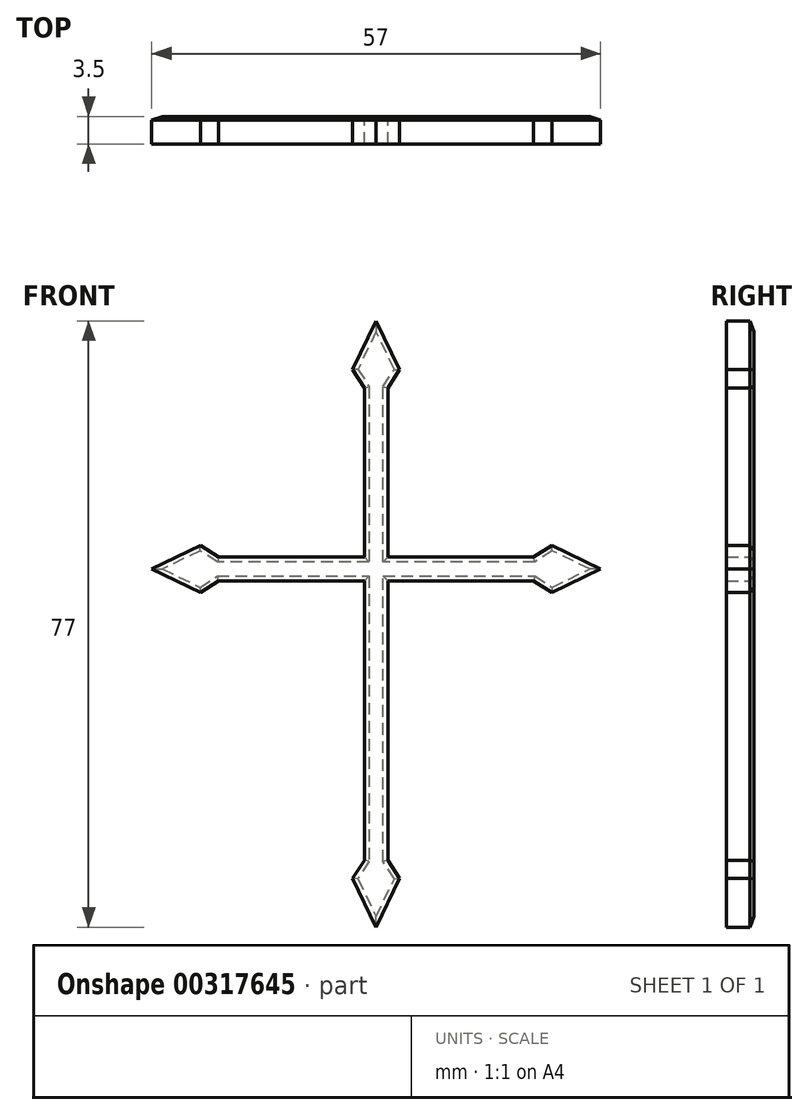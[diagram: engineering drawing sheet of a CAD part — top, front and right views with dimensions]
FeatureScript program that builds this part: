
annotation { "Feature Type Name" : "Feature", "Feature Type Description" : "" }
export const myFeature = defineFeature(function(context is Context, id is Id, definition is map)
    precondition{}
    {
        {
            var Q0;
            Q0=qCreatedBy(makeId("Front.planeOp"),FACE);
            var sketch = newSketch(context, id + "F0", { "sketchPlane" : qUnion([Q0])});
            skLineSegment(sketch, "E0", {"start": v(-20, 1.5) * mm, "end": v(-1.5, 1.5) * mm});
            skLineSegment(sketch, "E1.MirrorCS", {"start": v(-20, -1.5) * mm, "end": v(-1.5, -1.5) * mm});
            skLineSegment(sketch, "E2", {"start": v(-1.5, 23) * mm, "end": v(-1.5, 1.5) * mm});
            skLineSegment(sketch, "E3", {"start": v(1.5, -37) * mm, "end": v(1.5, -1.5) * mm});
            skLineSegment(sketch, "E4", {"start": v(20, -1.5) * mm, "end": v(22.33, -3) * mm});
            skLineSegment(sketch, "E5.MirrorCS", {"start": v(20, 1.5) * mm, "end": v(22.33, 3) * mm});
            skLineSegment(sketch, "E6", {"start": v(22.33, 3) * mm, "end": v(28.5, 0) * mm});
            skLineSegment(sketch, "E7.MirrorCS", {"start": v(22.33, -3) * mm, "end": v(28.5, 0) * mm});
            skLineSegment(sketch, "E8.MirrorCS", {"start": v(-20, 1.5) * mm, "end": v(-22.33, 3) * mm});
            skLineSegment(sketch, "E9.MirrorCS", {"start": v(-20, -1.5) * mm, "end": v(-22.33, -3) * mm});
            skLineSegment(sketch, "E10.MirrorCS", {"start": v(-22.33, -3) * mm, "end": v(-28.5, 0) * mm});
            skLineSegment(sketch, "E11.MirrorCS", {"start": v(-22.33, 3) * mm, "end": v(-28.5, 0) * mm});
            skLineSegment(sketch, "E12", {"start": v(-1.5, 23) * mm, "end": v(-3, 25.33) * mm});
            skLineSegment(sketch, "E13", {"start": v(-3, 25.33) * mm, "end": v(0, 31.5) * mm});
            skLineSegment(sketch, "E14.MirrorCS", {"start": v(1.5, 23) * mm, "end": v(3, 25.33) * mm});
            skLineSegment(sketch, "E15.MirrorCS", {"start": v(3, 25.33) * mm, "end": v(0, 31.5) * mm});
            skLineSegment(sketch, "E16", {"start": v(-20, -7) * mm, "end": v(19.26, -7) * mm, "construction": true});
            skLineSegment(sketch, "E17.MirrorCS", {"start": v(-1.5, -37) * mm, "end": v(-3, -39.33) * mm});
            skLineSegment(sketch, "E18.MirrorCS", {"start": v(-3, -39.33) * mm, "end": v(0, -45.5) * mm});
            skLineSegment(sketch, "E19.MirrorCS", {"start": v(3, -39.33) * mm, "end": v(0, -45.5) * mm});
            skLineSegment(sketch, "E20.MirrorCS", {"start": v(1.5, -37) * mm, "end": v(3, -39.33) * mm});
            skLineSegment(sketch, "E21.trimOffspring", {"start": v(-1.5, -1.5) * mm, "end": v(-1.5, -37) * mm});
            skLineSegment(sketch, "E22.trimOffspring", {"start": v(1.5, 1.5) * mm, "end": v(20, 1.5) * mm});
            skLineSegment(sketch, "E23.trimOffspring", {"start": v(1.5, 1.5) * mm, "end": v(1.5, 23) * mm});
            skLineSegment(sketch, "E24.trimOffspring", {"start": v(1.5, -1.5) * mm, "end": v(20, -1.5) * mm});
            skLineSegment(sketch, "E25", {"start": v(-1.5, -1) * mm, "end": v(-20, -1) * mm});
            skLineSegment(sketch, "E26.MirrorCS", {"start": v(-1.5, 1) * mm, "end": v(-20, 1) * mm});
            skLineSegment(sketch, "E27.MirrorCS", {"start": v(1.5, -1) * mm, "end": v(20, -1) * mm});
            skLineSegment(sketch, "E28.MirrorCS", {"start": v(1.5, 1) * mm, "end": v(20, 1) * mm});
            skLineSegment(sketch, "E29", {"start": v(-1, -1.5) * mm, "end": v(-1, -37) * mm});
            skLineSegment(sketch, "E30", {"start": v(-1, -37) * mm, "end": v(-2.5, -39.33) * mm});
            skLineSegment(sketch, "E31", {"start": v(-2.5, -39.33) * mm, "end": v(0, -44.47) * mm});
            skLineSegment(sketch, "E32", {"start": v(0, -44.47) * mm, "end": v(2.5, -39.33) * mm});
            skLineSegment(sketch, "E33", {"start": v(2.5, -39.33) * mm, "end": v(1, -37) * mm});
            skLineSegment(sketch, "E34", {"start": v(1, -37) * mm, "end": v(1, -1) * mm});
            skLineSegment(sketch, "E35", {"start": v(1, -1) * mm, "end": v(1.5, -1) * mm});
            skLineSegment(sketch, "E36", {"start": v(-1, -1.5) * mm, "end": v(-1, -1) * mm});
            skLineSegment(sketch, "E37", {"start": v(-1, -1) * mm, "end": v(-1.5, -1) * mm});
            skLineSegment(sketch, "E38", {"start": v(-20, -1) * mm, "end": v(-22.33, -2.5) * mm});
            skLineSegment(sketch, "E39", {"start": v(-22.33, -2.5) * mm, "end": v(-27.47, 0) * mm});
            skLineSegment(sketch, "E40", {"start": v(-27.47, 0) * mm, "end": v(-22.33, 2.5) * mm});
            skLineSegment(sketch, "E41", {"start": v(-22.33, 2.5) * mm, "end": v(-20, 1) * mm});
            skLineSegment(sketch, "E42", {"start": v(-1.5, 1) * mm, "end": v(-1, 1) * mm});
            skLineSegment(sketch, "E43", {"start": v(-1, 1) * mm, "end": v(-1, 23) * mm});
            skLineSegment(sketch, "E44", {"start": v(-1, 23) * mm, "end": v(-2.5, 25.33) * mm});
            skLineSegment(sketch, "E45", {"start": v(-2.5, 25.33) * mm, "end": v(0, 30.47) * mm});
            skLineSegment(sketch, "E46", {"start": v(0, 30.47) * mm, "end": v(2.5, 25.33) * mm});
            skLineSegment(sketch, "E47", {"start": v(2.5, 25.33) * mm, "end": v(1, 23) * mm});
            skLineSegment(sketch, "E48", {"start": v(1, 23) * mm, "end": v(1, 1) * mm});
            skLineSegment(sketch, "E49", {"start": v(1, 1) * mm, "end": v(1.5, 1) * mm});
            skLineSegment(sketch, "E50", {"start": v(20, 1) * mm, "end": v(22.33, 2.5) * mm});
            skLineSegment(sketch, "E51", {"start": v(22.33, 2.5) * mm, "end": v(27.47, 0) * mm});
            skLineSegment(sketch, "E52", {"start": v(27.47, 0) * mm, "end": v(22.33, -2.5) * mm});
            skLineSegment(sketch, "E53", {"start": v(22.33, -2.5) * mm, "end": v(20, -1) * mm});
            skSolve(sketch);
        }
        {
            var Q0;
            Q0=makeQuery(id+"F0.imprint","IMPRINT",FACE,{"disambiguationData":[TD([[makeQuery(id+"F0.imprint","IMPRINT",EDGE,{"derivedFrom":sQuery(id+"F0.wireOp",EDGE,"E25")}),-1.0]])]});
            var Q1;
            Q1=makeQuery(id+"F0.imprint","IMPRINT",FACE,{"disambiguationData":[TD([[makeQuery(id+"F0.imprint","IMPRINT",EDGE,{"derivedFrom":sQuery(id+"F0.wireOp",EDGE,"E0")}),-1.0]])]});
            extrude(context, id + "F1", {"entities" : qUnion([Q0, Q1]), "depth" : 1.5 * mm});
        }
        {
            var Q0;
            Q0=makeQuery(id+"F0.imprint","IMPRINT",FACE,{"disambiguationData":[TD([[makeQuery(id+"F0.imprint","IMPRINT",EDGE,{"derivedFrom":sQuery(id+"F0.wireOp",EDGE,"E0")}),-1.0]])]});
            var Q1;
            Q1=makeQuery(id+"F0.imprint","IMPRINT",FACE,{"disambiguationData":[TD([[makeQuery(id+"F0.imprint","IMPRINT",EDGE,{"derivedFrom":sQuery(id+"F0.wireOp",EDGE,"E25")}),-1.0]])]});
            extrude(context, id + "F2", {"entities" : qUnion([Q0, Q1]), "operationType" : NewBodyOperationType.ADD, "oppositeDirection" : true, "depth" : 0.5 * mm, "hasDraft" : true, "draftAngle" : 50 * degree, "draftPullDirection" : true});
        }
        {
            var Q0;
            Q0=makeQuery(id+"F1.opExtrude","CAP_FACE",FACE,{"disambiguationData":[OSD([sQuery(id+"F0.wireOp",EDGE,"E0"),sQuery(id+"F0.wireOp",EDGE,"E1.MirrorCS"),sQuery(id+"F0.wireOp",EDGE,"E2"),sQuery(id+"F0.wireOp",EDGE,"E3"),sQuery(id+"F0.wireOp",EDGE,"E4"),sQuery(id+"F0.wireOp",EDGE,"E5.MirrorCS"),sQuery(id+"F0.wireOp",EDGE,"E6"),sQuery(id+"F0.wireOp",EDGE,"E7.MirrorCS"),sQuery(id+"F0.wireOp",EDGE,"E8.MirrorCS"),sQuery(id+"F0.wireOp",EDGE,"E9.MirrorCS"),sQuery(id+"F0.wireOp",EDGE,"E10.MirrorCS"),sQuery(id+"F0.wireOp",EDGE,"E11.MirrorCS"),sQuery(id+"F0.wireOp",EDGE,"E12"),sQuery(id+"F0.wireOp",EDGE,"E13"),sQuery(id+"F0.wireOp",EDGE,"E14.MirrorCS"),sQuery(id+"F0.wireOp",EDGE,"E15.MirrorCS"),sQuery(id+"F0.wireOp",EDGE,"E17.MirrorCS"),sQuery(id+"F0.wireOp",EDGE,"E18.MirrorCS"),sQuery(id+"F0.wireOp",EDGE,"E19.MirrorCS"),sQuery(id+"F0.wireOp",EDGE,"E20.MirrorCS"),sQuery(id+"F0.wireOp",EDGE,"E21.trimOffspring"),sQuery(id+"F0.wireOp",EDGE,"E22.trimOffspring"),sQuery(id+"F0.wireOp",EDGE,"E23.trimOffspring"),sQuery(id+"F0.wireOp",EDGE,"E24.trimOffspring")])],"isStart":false});
            extrude(context, id + "F3", {"entities" : qUnion([Q0]), "operationType" : NewBodyOperationType.ADD, "depth" : 1.5 * mm});
        }
    });
